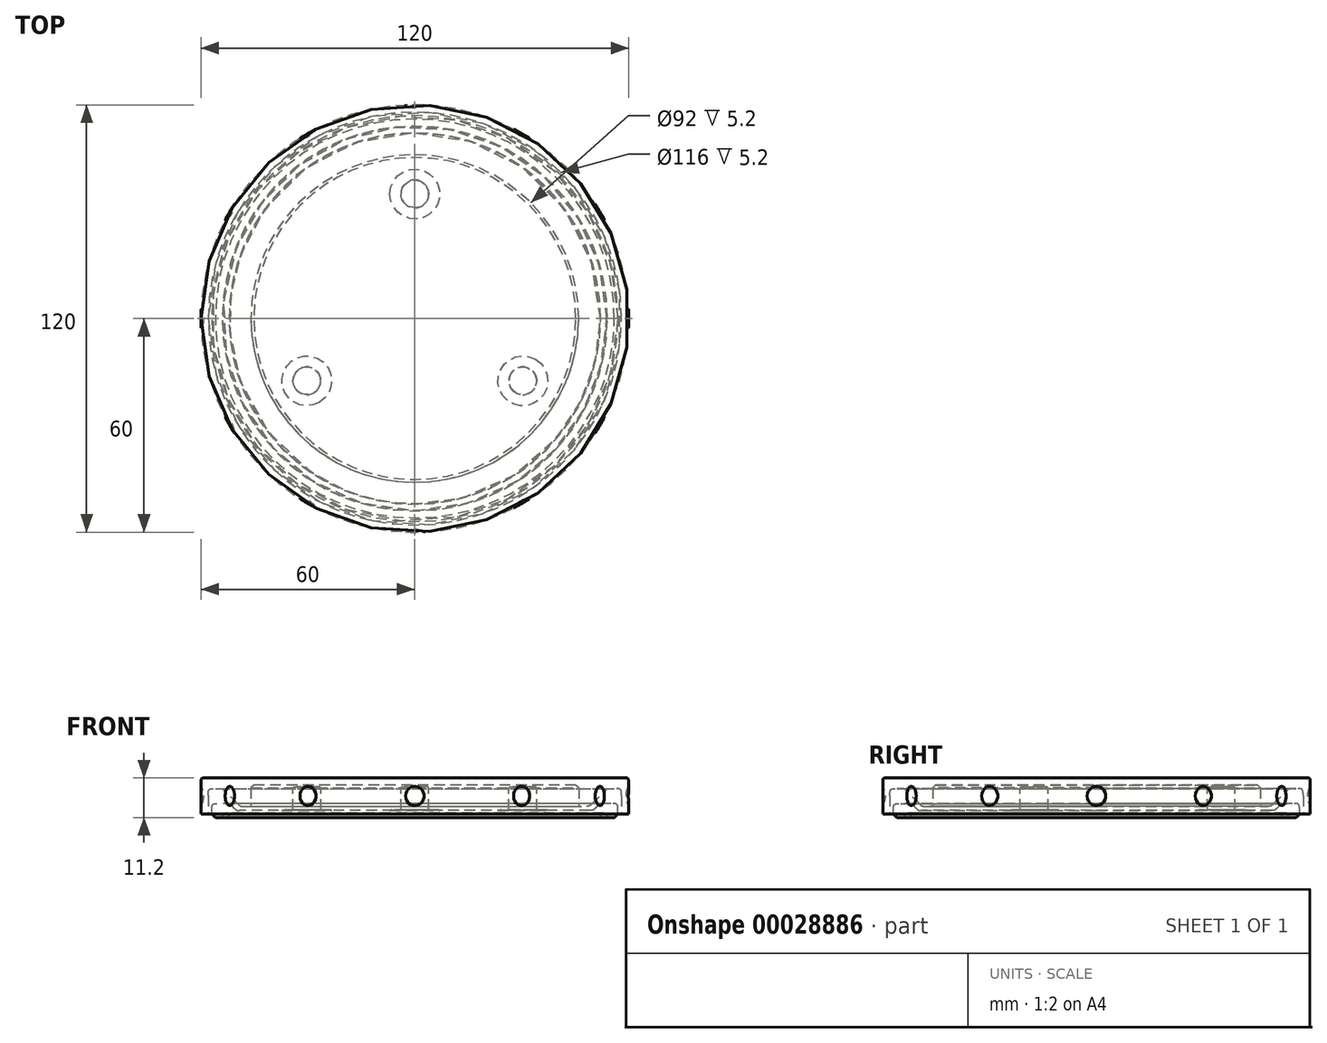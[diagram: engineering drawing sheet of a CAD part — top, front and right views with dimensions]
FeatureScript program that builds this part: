
annotation { "Feature Type Name" : "Feature", "Feature Type Description" : "" }
export const myFeature = defineFeature(function(context is Context, id is Id, definition is map)
    precondition{}
    {
        {
            var Q0;
            Q0=qCreatedBy(makeId("Top.planeOp"),FACE);
            var sketch = newSketch(context, id + "F0", { "sketchPlane" : qUnion([Q0])});
            skCircle(sketch, "E0", {"center": v(0, 0) * mm, "radius": 60 * mm, "construction": true});
            skSolve(sketch);
        }
        {
            var Q0;
            Q0=qCreatedBy(makeId("Right.planeOp"),FACE);
            var sketch = newSketch(context, id + "F1", { "sketchPlane" : qUnion([Q0])});
            skLineSegment(sketch, "E1", {"start": v(0, 0) * mm, "end": v(57, 0) * mm});
            skLineSegment(sketch, "E2", {"start": v(57, 0) * mm, "end": v(57, 4) * mm});
            skLineSegment(sketch, "E3", {"start": v(57, 4) * mm, "end": v(52, 4) * mm});
            skLineSegment(sketch, "E4", {"start": v(50, 2) * mm, "end": v(0, 2) * mm});
            skLineSegment(sketch, "E5", {"start": v(57, 0) * mm, "end": v(60, 0) * mm, "construction": true});
            skLineSegment(sketch, "E6", {"start": v(52, 4) * mm, "end": v(50, 2) * mm});
            skLineSegment(sketch, "E7", {"start": v(0, 2) * mm, "end": v(0, 0) * mm});
            skSolve(sketch);
        }
        {
            var Q0;
            Q0=qSketchRegion(id+"F1",true);
            var Q1;
            Q1=sQuery(id+"F1.wireOp",EDGE,"E7");
            revolve(context, id + "F2", {"entities" : qUnion([Q0]), "axis" : qUnion([Q1]), "revolveType" : RevolveType.FULL});
        }
        {
            var Q0;
            Q0=qCreatedBy(makeId("Right.planeOp"),FACE);
            var sketch = newSketch(context, id + "F3", { "sketchPlane" : qUnion([Q0])});
            skLineSegment(sketch, "E8", {"start": v(35, 2) * mm, "end": v(42, 2) * mm});
            skLineSegment(sketch, "E9", {"start": v(42, 2) * mm, "end": v(42, 2.2) * mm});
            skLineSegment(sketch, "E10", {"start": v(42, 2.2) * mm, "end": v(38.9, 2.2) * mm});
            skLineSegment(sketch, "E11", {"start": v(38.9, 2.2) * mm, "end": v(38.9, 8.7) * mm});
            skLineSegment(sketch, "E12", {"start": v(38.9, 8.7) * mm, "end": v(35, 8.7) * mm});
            skLineSegment(sketch, "E13", {"start": v(35, 8.7) * mm, "end": v(35, 2) * mm});
            skLineSegment(sketch, "E14", {"start": v(35, 2) * mm, "end": v(35, 0) * mm, "construction": true});
            skLineSegment(sketch, "E15", {"start": v(35, 0) * mm, "end": v(60, 0) * mm, "construction": true});
            skSolve(sketch);
        }
        {
            var Q0;
            Q0 = qSketchRegion(id + "F3", true);
            var Q1;
            Q1=sQuery(id+"F3.wireOp",EDGE,"E13");
            revolve(context, id + "F4", {"operationType" : NewBodyOperationType.ADD, "entities" : qUnion([Q0]), "axis" : qUnion([Q1]), "revolveType" : RevolveType.FULL});
        }
        {
            var Q0;
            Q0=makeQuery(id+"F4.opRevolve","SWEPT_EDGE",EDGE,{"disambiguationData":[OSD([sQuery(id+"F3.wireOp",EDGE,"E11"),sQuery(id+"F3.wireOp",EDGE,"E12")])]});
            var Q1;
            Q1=makeQuery(id+"F4.opRevolve","SWEPT_EDGE",EDGE,{"disambiguationData":[OSD([sQuery(id+"F3.wireOp",EDGE,"E9"),sQuery(id+"F3.wireOp",EDGE,"E10")])]});
            fillet(context, id + "F5", {"entities" : qUnion([Q0, Q1]), "radius" : 1 * mm, "tangentPropagation" : true, "rho" : .7, "crossSection" : FilletCrossSection.CONIC, "allowEdgeOverflow" : false});
        }
        {
            var Q0;
            Q0=qCreatedBy(makeId("Right.planeOp"),FACE);
            var sketch = newSketch(context, id + "F6", { "sketchPlane" : qUnion([Q0])});
            skLineSegment(sketch, "E16", {"start": v(0, 0) * mm, "end": v(0, 45.85) * mm});
            skSolve(sketch);
        }
        {
            var Q0;
            Q0=makeQuery(id+"F2.opRevolve","SWEPT_BODY",BODY,{"disambiguationData":[OSD([sQuery(id+"F1.wireOp",EDGE,"E1"),sQuery(id+"F1.wireOp",EDGE,"E2"),sQuery(id+"F1.wireOp",EDGE,"E3"),sQuery(id+"F1.wireOp",EDGE,"E4"),sQuery(id+"F1.wireOp",EDGE,"E6"),sQuery(id+"F1.wireOp",EDGE,"E7")])]});
            var Q1;
            Q1=makeQuery(id+"F4.opRevolve","SWEPT_FACE",FACE,{"disambiguationData":[OSD([sQuery(id+"F3.wireOp",EDGE,"E10")])]});
            var Q2;
            Q2=makeQuery(id+"F4.opRevolve","SWEPT_FACE",FACE,{"disambiguationData":[OSD([sQuery(id+"F3.wireOp",EDGE,"E12")])]});
            var Q3;
            Q3=makeQuery(id+"F5.opFillet","BLEND_FACE",FACE,{"disambiguationData":[OSD([sQuery(id+"F3.wireOp",EDGE,"E11"),sQuery(id+"F3.wireOp",EDGE,"E12")])]});
            var Q4;
            Q4=makeQuery(id+"F4.opRevolve","SWEPT_FACE",FACE,{"disambiguationData":[OSD([sQuery(id+"F3.wireOp",EDGE,"E11")])]});
            var Q5;
            Q5=makeQuery(id+"F5.opFillet","BLEND_FACE",FACE,{"disambiguationData":[OSD([sQuery(id+"F3.wireOp",EDGE,"E9"),sQuery(id+"F3.wireOp",EDGE,"E10")])]});
            var Q6;
            Q6=sQuery(id+"F6.wireOp",EDGE,"E16");
            circularPattern(context, id + "F7", {"operationType" : NewBodyOperationType.ADD, "entities" : qUnion([Q0]), "axis" : qUnion([Q6]), "angle" : 360 * degree, "instanceCount" : 3, "equalSpace" : true});
        }
        {
            var Q0;
            Q0=makeQuery(id+"F2.opRevolve","SWEPT_FACE",FACE,{"disambiguationData":[OSD([sQuery(id+"F1.wireOp",EDGE,"E1")])]});
            var sketch = newSketch(context, id + "F8", { "sketchPlane" : qUnion([Q0])});
            skCircle(sketch, "E17", {"center": v(0, 0) * mm, "radius": 53 * mm});
            skSolve(sketch);
        }
        {
            var Q0;
            Q0=qCreatedBy(makeId("Right.planeOp"),FACE);
            var sketch = newSketch(context, id + "F9", { "sketchPlane" : qUnion([Q0])});
            skCircle(sketch, "E18", {"center": v(-53, 0.4) * mm, "radius": 0.9 * mm});
            skLineSegment(sketch, "E19", {"start": v(-53, 0.4) * mm, "end": v(-53, 0) * mm, "construction": true});
            skLineSegment(sketch, "E20", {"start": v(-53, 0) * mm, "end": v(-53, -0.5) * mm, "construction": true});
            skSolve(sketch);
        }
        {
            var Q0;
            Q0 = qSketchRegion(id + "F9", true);
            var Q1;
            Q1=sQuery(id+"F8.wireOp",EDGE,"E17");
            sweep(context, id + "F10", {"operationType" : NewBodyOperationType.REMOVE, "profiles" : qUnion([Q0]), "path" : qUnion([Q1])});
        }
        {
            var Q0;
            Q0=qCreatedBy(makeId("Right.planeOp"),FACE);
            var sketch = newSketch(context, id + "F11", { "sketchPlane" : qUnion([Q0])});
            skLineSegment(sketch, "E21", {"start": v(0, 9.2) * mm, "end": v(0, 11.2) * mm});
            skLineSegment(sketch, "E22", {"start": v(0, 11.2) * mm, "end": v(60, 11.2) * mm});
            skLineSegment(sketch, "E23", {"start": v(60, 11.2) * mm, "end": v(60, 1) * mm});
            skLineSegment(sketch, "E24", {"start": v(60, 1) * mm, "end": v(58, 1) * mm});
            skLineSegment(sketch, "E25", {"start": v(58, 1) * mm, "end": v(58, 8.2) * mm});
            skLineSegment(sketch, "E26", {"start": v(58, 8.2) * mm, "end": v(54, 8.2) * mm});
            skLineSegment(sketch, "E27", {"start": v(54, 8.2) * mm, "end": v(49, 3.2) * mm});
            skLineSegment(sketch, "E28", {"start": v(49, 3.2) * mm, "end": v(46, 3.2) * mm});
            skLineSegment(sketch, "E29", {"start": v(46, 3.2) * mm, "end": v(46, 9.2) * mm});
            skLineSegment(sketch, "E30", {"start": v(46, 9.2) * mm, "end": v(0, 9.2) * mm});
            skLineSegment(sketch, "E31", {"start": v(60, 1) * mm, "end": v(60, 0) * mm, "construction": true});
            skLineSegment(sketch, "E32", {"start": v(46, 3.2) * mm, "end": v(46, 0) * mm, "construction": true});
            skLineSegment(sketch, "E33", {"start": v(46, 0) * mm, "end": v(60, 0) * mm, "construction": true});
            skSolve(sketch);
        }
        {
            var Q0;
            Q0=qSketchRegion(id+"F11",true);
            var Q1;
            Q1=sQuery(id+"F11.wireOp",EDGE,"E21");
            revolve(context, id + "F12", {"entities" : qUnion([Q0]), "axis" : qUnion([Q1]), "revolveType" : RevolveType.FULL});
        }
        {
            var Q0;
            Q0=makeQuery(id+"F2.opRevolve","SWEPT_EDGE",EDGE,{"disambiguationData":[OSD([sQuery(id+"F1.wireOp",EDGE,"E3"),sQuery(id+"F1.wireOp",EDGE,"E6")])]});
            var Q1;
            Q1=makeQuery(id+"F2.opRevolve","SWEPT_EDGE",EDGE,{"disambiguationData":[OSD([sQuery(id+"F1.wireOp",EDGE,"E4"),sQuery(id+"F1.wireOp",EDGE,"E6")])]});
            var Q2;
            Q2=makeQuery(id+"F2.opRevolve","SWEPT_EDGE",EDGE,{"disambiguationData":[OSD([sQuery(id+"F1.wireOp",EDGE,"E2"),sQuery(id+"F1.wireOp",EDGE,"E3")])]});
            fillet(context, id + "F13", {"entities" : qUnion([Q0, Q1, Q2]), "radius" : 2 * mm, "tangentPropagation" : true, "rho" : .7, "crossSection" : FilletCrossSection.CONIC, "allowEdgeOverflow" : false});
        }
        {
            var Q0;
            Q0=makeQuery(id+"F12.opRevolve","SWEPT_EDGE",EDGE,{"disambiguationData":[OSD([sQuery(id+"F11.wireOp",EDGE,"E25"),sQuery(id+"F11.wireOp",EDGE,"E26")])]});
            var Q1;
            Q1=makeQuery(id+"F12.opRevolve","SWEPT_EDGE",EDGE,{"disambiguationData":[OSD([sQuery(id+"F11.wireOp",EDGE,"E26"),sQuery(id+"F11.wireOp",EDGE,"E27")])]});
            var Q2;
            Q2=makeQuery(id+"F12.opRevolve","SWEPT_EDGE",EDGE,{"disambiguationData":[OSD([sQuery(id+"F11.wireOp",EDGE,"E27"),sQuery(id+"F11.wireOp",EDGE,"E28")])]});
            fillet(context, id + "F14", {"entities" : qUnion([Q0, Q1, Q2]), "radius" : 2 * mm, "tangentPropagation" : true, "rho" : .7, "crossSection" : FilletCrossSection.CONIC, "allowEdgeOverflow" : false});
        }
        {
            var Q0;
            Q0=makeQuery(id+"F12.opRevolve","SWEPT_EDGE",EDGE,{"disambiguationData":[OSD([sQuery(id+"F11.wireOp",EDGE,"E29"),sQuery(id+"F11.wireOp",EDGE,"E30")])]});
            chamfer(context, id + "F15", {"entities" : qUnion([Q0]), "width" : .8 * mm, "tangentPropagation" : true});
        }
        {
            var Q0;
            Q0=makeQuery(id+"F12.opRevolve","SWEPT_EDGE",EDGE,{"disambiguationData":[OSD([sQuery(id+"F11.wireOp",EDGE,"E22"),sQuery(id+"F11.wireOp",EDGE,"E23")])]});
            fillet(context, id + "F16", {"entities" : qUnion([Q0]), "radius" : 1 * mm, "tangentPropagation" : true, "rho" : .6, "crossSection" : FilletCrossSection.CONIC, "allowEdgeOverflow" : false});
        }
        {
            var Q0;
            Q0=makeQuery(id+"F10.boolean.opBoolean","INTERSECT",EDGE,{"disambiguationData":[OD(1.0)],"derivedFrom":[makeQuery(id+"F2.opRevolve","SWEPT_FACE",FACE,{"disambiguationData":[OSD([sQuery(id+"F1.wireOp",EDGE,"E1")])]}),makeQuery(id+"F10.opSweep","SWEPT_FACE",FACE,{"disambiguationData":[OSD([sQuery(id+"F8.wireOp",EDGE,"E17"),sQuery(id+"F9.wireOp",EDGE,"E18")])]})]});
            var Q1;
            Q1=makeQuery(id+"F10.boolean.opBoolean","INTERSECT",EDGE,{"disambiguationData":[OD(0.0)],"derivedFrom":[makeQuery(id+"F2.opRevolve","SWEPT_FACE",FACE,{"disambiguationData":[OSD([sQuery(id+"F1.wireOp",EDGE,"E1")])]}),makeQuery(id+"F10.opSweep","SWEPT_FACE",FACE,{"disambiguationData":[OSD([sQuery(id+"F8.wireOp",EDGE,"E17"),sQuery(id+"F9.wireOp",EDGE,"E18")])]})]});
            chamfer(context, id + "F17", {"entities" : qUnion([Q0, Q1]), "chamferType" : ChamferType.OFFSET_ANGLE, "width" : .1 * mm, "oppositeDirection" : true, "angle" : 90 * degree, "tangentPropagation" : true});
        }
        {
            var Q0;
            Q0=makeQuery(id+"F2.opRevolve","SWEPT_EDGE",EDGE,{"disambiguationData":[OSD([sQuery(id+"F1.wireOp",EDGE,"E1"),sQuery(id+"F1.wireOp",EDGE,"E2")])]});
            chamfer(context, id + "F18", {"entities" : qUnion([Q0]), "width" : 1 * mm, "tangentPropagation" : true});
        }
        {
            var Q0;
            Q0=qCreatedBy(makeId("Right.planeOp"),FACE);
            var sketch = newSketch(context, id + "F19", { "sketchPlane" : qUnion([Q0])});
            skLineSegment(sketch, "E34", {"start": v(64.2, 11.1) * mm, "end": v(64.2, 1.1) * mm});
            skLineSegment(sketch, "E35", {"start": v(64.2, 1.1) * mm, "end": v(64.2, 0) * mm, "construction": true});
            skLineSegment(sketch, "E36", {"start": v(64.2, 0) * mm, "end": v(60, 0) * mm, "construction": true});
            skLineSegment(sketch, "E37", {"start": v(64.2, 6.1) * mm, "end": v(59, 6.1) * mm, "construction": true});
            skLineSegment(sketch, "E38", {"start": v(59, 11.2) * mm, "end": v(59, 1) * mm, "construction": true});
            skArc(sketch, "E39", {"start": v(64.2, 11.1) * mm, "mid": v(59.2, 6.1) * mm, "end": v(64.2, 1.1) * mm});
            skSolve(sketch);
        }
        {
            var Q0;
            Q0=makeQuery(id+"F19.imprint","IMPRINT",FACE,{"disambiguationData":[TD([[makeQuery(id+"F19.imprint","IMPRINT",EDGE,{"derivedFrom":sQuery(id+"F19.wireOp",EDGE,"E34")}),-1.0]])]});
            var Q1;
            Q1=sQuery(id+"F19.wireOp",EDGE,"E34");
            revolve(context, id + "F20", {"operationType" : NewBodyOperationType.REMOVE, "entities" : qUnion([Q0]), "axis" : qUnion([Q1]), "revolveType" : RevolveType.FULL, "oppositeDirection" : true});
        }
        {
            var Q0;
            Q0=makeQuery(id+"F12.opRevolve","SWEPT_BODY",BODY,{"disambiguationData":[OSD([sQuery(id+"F11.wireOp",EDGE,"E21"),sQuery(id+"F11.wireOp",EDGE,"E22"),sQuery(id+"F11.wireOp",EDGE,"E23"),sQuery(id+"F11.wireOp",EDGE,"E24"),sQuery(id+"F11.wireOp",EDGE,"E25"),sQuery(id+"F11.wireOp",EDGE,"E26"),sQuery(id+"F11.wireOp",EDGE,"E27"),sQuery(id+"F11.wireOp",EDGE,"E28"),sQuery(id+"F11.wireOp",EDGE,"E29"),sQuery(id+"F11.wireOp",EDGE,"E30")])]});
            var Q1;
            Q1=makeQuery(id+"F20.boolean.opBoolean","COPY",FACE,{"derivedFrom":makeQuery(id+"F20.opRevolve","SWEPT_FACE",FACE,{"disambiguationData":[OSD([sQuery(id+"F19.wireOp",EDGE,"E39")])]})});
            var Q2;
            Q2=sQuery(id+"F6.wireOp",EDGE,"E16");
            circularPattern(context, id + "F21", {"faces" : qUnion([Q1]), "axis" : qUnion([Q2]), "angle" : 360 * degree, "instanceCount" : 12, "equalSpace" : true, "patternType" : PatternType.FACE});
        }
    });
